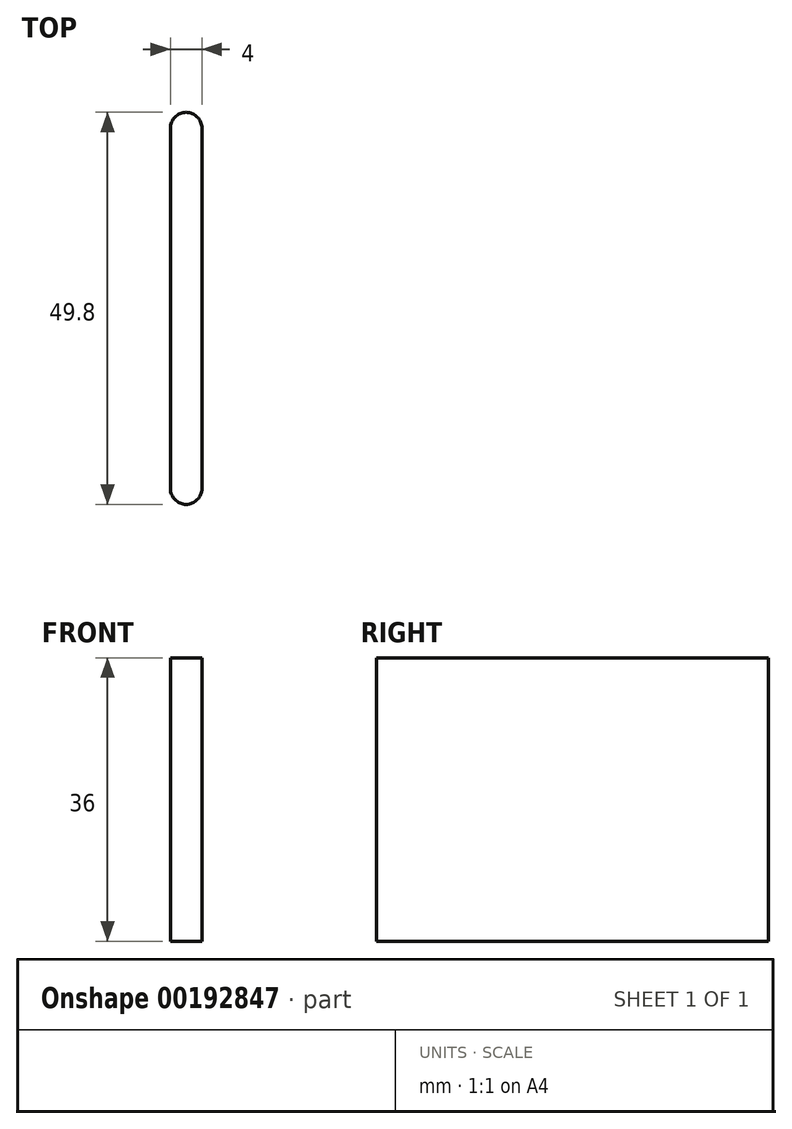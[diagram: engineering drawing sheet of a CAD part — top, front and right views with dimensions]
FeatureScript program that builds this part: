
annotation { "Feature Type Name" : "Feature", "Feature Type Description" : "" }
export const myFeature = defineFeature(function(context is Context, id is Id, definition is map)
    precondition{}
    {
        {
            var Q0;
            Q0=qCreatedBy(makeId("Top.planeOp"),FACE);
            var sketch = newSketch(context, id + "F0", { "sketchPlane" : qUnion([Q0])});
            skArc(sketch, "E0", {"start": v(2, 22.4) * mm, "mid": v(0, 24.4) * mm, "end": v(-2, 22.4) * mm});
            skArc(sketch, "E1", {"start": v(-2, -23.4) * mm, "mid": v(0, -25.4) * mm, "end": v(2, -23.4) * mm});
            skLineSegment(sketch, "E2", {"start": v(2, 22.4) * mm, "end": v(2, -23.4) * mm});
            skLineSegment(sketch, "E3", {"start": v(-2, 22.4) * mm, "end": v(-2, -23.4) * mm});
            skSolve(sketch);
        }
        {
            var Q0;
            Q0=makeQuery(id+"F0.imprint","IMPRINT",FACE,{"disambiguationData":[TD([[makeQuery(id+"F0.imprint","IMPRINT",EDGE,{"derivedFrom":sQuery(id+"F0.wireOp",EDGE,"E0")}),1.0]])]});
            extrude(context, id + "F1", {"entities" : qUnion([Q0]), "depth" : 36 * mm, "symmetric" : true});
        }
    });
